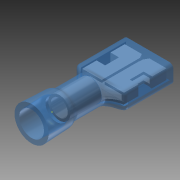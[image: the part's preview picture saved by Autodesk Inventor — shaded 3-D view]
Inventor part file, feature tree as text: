
AUTODESK INVENTOR PART (.ipt)
format: ipt  version: 2014 (Build 180170000, 170)  size: 611,840 bytes
history: native  units: in
note: dims shown in document units (in); Inventor stores cm internally (conversion verified against a paired STEP export)
features: sketch x20, projected_geometry x16, extrude x13, fillet x4, plane x3, loft x3, shell x1, revolve x1, chamfer x1
ambient origin geometry x8: Origin, YZ Plane, XZ Plane, XY Plane, X Axis, Y Axis, Z Axis, Center Point
bodies: Solid1 (feature_tree), Solid2 (feature_tree)
feature tree (62):
  extrude  "Extrusion1"  Depth=0.259in TaperAngle=0.0deg
  extrude  "Extrusion2"  Depth=0.254in TaperAngle=0.0deg
  extrude  "Extrusion3"  Depth=0.033in TaperAngle=0.0deg
  shell  "Shell1"  Thickness=0.0185in
  extrude  "Extrusion4"  Depth=0.0185in
  revolve  "Revolution1"  [1 undecoded]
  plane  "Work Plane1"
  sketch  "Sketch6"  dims[d15=0.4in d16=0.018in]
  plane  "Work Plane2"
  extrude  "Extrusion5"  Depth=0.018in
  loft  "Loft1"
  fillet  "Fillet1"  Radius=0.018in
  extrude  "Extrusion6"  Depth=0.018in
  extrude  "Extrusion7"  Depth=0.3937in TaperAngle=0.0deg
  chamfer  "Chamfer1"  Distance=0.3937in Angle=90.0deg
  plane  "Work Plane3"
  extrude  "Extrusion8"  Depth=0.02in
  sketch  "Sketch14"  dims[d45=0.01in d46=0.01in]
  sketch  "Sketch13"  dims[d41=0.003in d42=0.125in d43=45.0deg d44=0.02in]
  loft  "Loft2"
  loft  "Loft3"
  fillet  "Fillet2"  Radius=0.02in
  extrude  "Extrusion9"  Depth=0.01in
  extrude  "Extrusion10"  Depth=0.01in
  sketch  "Sketch18"  dims[d51=1.0in d52=0.0in d57=0.3937in d58=90.0deg]
  sketch  "Sketch19"  dims[d59=0.3937in d60=90.0deg d61=0.0in d62=90.0deg d63=0.0in d64=90.0deg d65=0.02in]
  extrude  "Extrusion11"  Depth=0.02in
  extrude  "Extrusion12"  Depth=0.3937in TaperAngle=90.0deg
  extrude  "Extrusion13"  TaperAngle=0.0deg  [1 undecoded]
  fillet  "Fillet3"  [1 undecoded]
  fillet  "Fillet4"  Radius=0.02in
  sketch  "Sketch1"  dims[d0=0.1965in d1=0.259in d2=0.0in]
  sketch  "Sketch2"  dims[d3=0.204in d4=0.254in d5=0.0in]
  projected_geometry  "Projected Loop1"
  sketch  "Sketch3"  dims[d6=0.23in d7=0.033in d8=0.0in d9=0.0185in]
  projected_geometry  "Projected Loop2"
  sketch  "Sketch4"  dims[d10=0.033in d11=0.0in d12=0.0185in]
  projected_geometry  "Projected Loop3"
  sketch  "Sketch5"  dims[d13=90.0deg d14=-0.0625in]
  sketch  "Sketch7"  dims[d17=0.3015in d18=0.018in d19=0.018in]
  sketch  "Sketch8"  dims[d20=0.018in d21=0.037in]
  projected_geometry  "Projected Loop4"
  sketch  "Sketch9"  dims[d22=0.02in d23=0.307in d24=0.0in d29=0.3937in d30=90.0deg]
  projected_geometry  "Projected Loop5"
  sketch  "Sketch10"  dims[d31=0.0in d32=90.0deg d33=0.02in]
  projected_geometry  "Projected Loop6"
  projected_geometry  "Projected Loop7"
  sketch  "Sketch11"  dims[d34=0.1in d36=0.178in]
  projected_geometry  "Projected Loop8"
  projected_geometry  "Projected Loop9"
  sketch  "Sketch12"  dims[d37=0.307in d38=0.0in d39=0.05in d40=0.0in]
  projected_geometry  "Projected Loop10"
  projected_geometry  "Projected Loop11"
  sketch  "Sketch15"  dims[d47=0.01in d48=0.01in]
  projected_geometry  "Projected Loop12"
  sketch  "Sketch17"  dims[d49=0.01in d50=0.02in]
  projected_geometry  "Projected Loop14"
  sketch  "Sketch20"  dims[d66=0.3in d67=0.0in]
  sketch  "Sketch21"  dims[d68=0.2in d69=0.0in d70=0.2in d71=0.0in d72=0.2in d73=0.0172in d74=0.02in d75=0.0in d76=0.05in d77=0.05in]
  projected_geometry  "Projected Loop15"
  projected_geometry  "Project Cut Edges1"
  projected_geometry  "Project Cut Edges2"
note: 3 required parameter values undecoded (feature->parameter linkage not recoverable at this tier; creation-order binding heuristic only, values carry confidence <= 0.55)